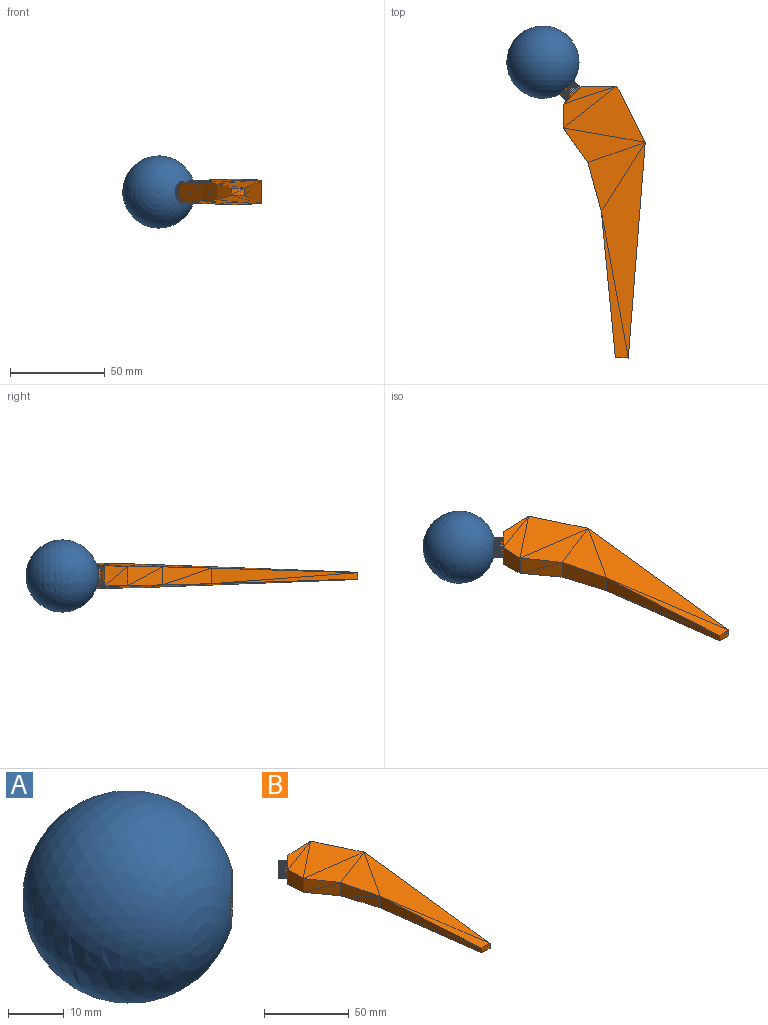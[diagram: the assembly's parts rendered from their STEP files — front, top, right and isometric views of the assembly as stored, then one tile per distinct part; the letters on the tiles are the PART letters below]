
ASSEMBLY  parts=2 mates=1
PART A: 119 faces, bbox 38.1x38.1x38.1 mm
  f0: sphere r=19.05mm, area 4472mm2, adj f2,f3,f4,f5,f6,f7,f8,f9
  f1: plane 10.52x7.44mm, normal (0.71,-0.71,0), area 86.6mm2, adj f2,f3,f4,f5,f6,f7,f8,f9
  f2: plane 0.64x0.63mm, normal (0.69,0.69,0.21), area 0.4mm2, adj f0,f1,f3,f48
  f3: plane 0.58x0.57mm, normal (0.69,0.69,0.21), area 0.1mm2, adj f0,f1,f2,f4
  f4: plane 0.58x0.55mm, normal (0.67,0.67,0.33), area 0mm2, adj f0,f1,f3,f5
  f5: plane 0.75x0.72mm, normal (0.66,0.66,0.35), area 0.5mm2, adj f0,f1,f4,f6
  f6: plane 0.6x0.56mm, normal (0.62,0.62,0.49), area 0mm2, adj f0,f1,f5,f8
  f7: plane 0.84x0.81mm, normal (0.57,0.57,0.6), area 0.5mm2, adj f0,f1,f9,f45
  f8: plane 0.61x0.53mm, normal (0.65,0.68,0.35), area 0mm2, adj f0,f1,f6,f10
  f9: plane 0.62x0.61mm, normal (0.57,0.57,0.6), area 0.1mm2, adj f0,f1,f7,f10
  f10: plane 0.84x0.78mm, normal (0.62,0.62,0.48), area 0.6mm2, adj f0,f1,f8,f9
  f11: plane 0.85x0.82mm, normal (-0.05,-0.05,1), area 0.2mm2, adj f0,f1,f12,f30
  f12: plane 1.07x1.01mm, normal (-0.05,-0.05,1), area 0.5mm2, adj f0,f1,f11,f13
  f13: plane 0.76x0.75mm, normal (-0.09,-0.09,0.99), area 0.1mm2, adj f0,f1,f12,f14
  f14: plane 0.97x0.91mm, normal (-0.15,-0.15,0.98), area 0.3mm2, adj f0,f1,f13,f15
  f15: plane 0.98x0.94mm, normal (-0.15,-0.15,0.98), area 0.4mm2, adj f0,f1,f14,f16
  f16: plane 0.78x0.77mm, normal (-0.21,-0.2,0.96), area 0.1mm2, adj f0,f1,f15,f17
  f17: plane 1.07x1mm, normal (-0.25,-0.25,0.94), area 0.5mm2, adj f0,f1,f16,f18
  f18: plane 0.89x0.87mm, normal (-0.25,-0.25,0.94), area 0.2mm2, adj f0,f1,f17,f19
  f19: plane 0.81x0.77mm, normal (-0.32,-0.32,0.89), area 0.1mm2, adj f0,f1,f18,f20
  f20: plane 1.16x1.07mm, normal (-0.34,-0.34,0.88), area 0.6mm2, adj f0,f1,f19,f22
  f21: plane 1.02x0.99mm, normal (-0.56,-0.57,0.6), area 0.6mm2, adj f0,f1,f23,f101
  f22: plane 0.81x0.8mm, normal (-0.34,-0.34,0.88), area 0.1mm2, adj f0,f1,f20,f24
  f23: plane 0.86x0.84mm, normal (-0.56,-0.57,0.6), area 0.2mm2, adj f0,f1,f21,f25
  f24: plane 0.84x0.76mm, normal (-0.42,-0.42,0.8), area 0.1mm2, adj f0,f1,f22,f26
  f25: plane 0.85x0.8mm, normal (-0.51,-0.51,0.69), area 0.1mm2, adj f0,f1,f23,f27
  f26: plane 1.2x1.11mm, normal (-0.42,-0.42,0.8), area 0.7mm2, adj f0,f1,f24,f28
  f27: plane 1.13x1.07mm, normal (-0.5,-0.5,0.71), area 0.7mm2, adj f0,f1,f25,f28
  f28: plane 0.79x0.78mm, normal (-0.5,-0.5,0.71), area 0mm2, adj f0,f1,f26,f27
  f29: plane 1.14x1.08mm, normal (0.05,0.05,1), area 0.6mm2, adj f0,f1,f30,f31
  f30: plane 0.76x0.71mm, normal (0.03,0.03,1), area 0.1mm2, adj f0,f1,f11,f29
  f31: plane 0.73x0.71mm, normal (0.05,0.05,1), area 0.1mm2, adj f0,f1,f29,f34
  f32: plane 1.17x1.09mm, normal (0.15,0.15,0.98), area 0.6mm2, adj f0,f1,f33,f34
  f33: plane 0.69x0.68mm, normal (0.25,0.25,0.94), area 0.1mm2, adj f0,f1,f32,f35
  f34: plane 0.75x0.68mm, normal (0.15,0.15,0.98), area 0.1mm2, adj f0,f1,f31,f32
  f35: plane 1.1x1.02mm, normal (0.25,0.25,0.94), area 0.6mm2, adj f0,f1,f33,f39
  f36: plane 0.75x0.73mm, normal (0.34,0.34,0.88), area 0.2mm2, adj f0,f1,f37,f39
  f37: plane 0.97x0.9mm, normal (0.34,0.34,0.88), area 0.4mm2, adj f0,f1,f36,f41
  f38: plane 0.8x0.78mm, normal (0.43,0.42,0.8), area 0.3mm2, adj f0,f1,f40,f41
  f39: plane 0.7x0.65mm, normal (0.26,0.27,0.93), area 0.1mm2, adj f0,f1,f35,f36
  f40: plane 0.84x0.8mm, normal (0.43,0.42,0.8), area 0.3mm2, adj f0,f1,f38,f43
  f41: plane 0.66x0.64mm, normal (0.37,0.37,0.85), area 0.1mm2, adj f0,f1,f37,f38
  f42: plane 0.83x0.8mm, normal (0.5,0.5,0.71), area 0.4mm2, adj f0,f1,f43,f44
  f43: plane 0.63x0.63mm, normal (0.46,0.47,0.75), area 0.1mm2, adj f0,f1,f40,f42
  f44: plane 0.72x0.7mm, normal (0.5,0.5,0.71), area 0.2mm2, adj f0,f1,f42,f45
  f45: plane 0.62x0.6mm, normal (0.55,0.55,0.63), area 0.1mm2, adj f0,f1,f7,f44
  f46: plane 0.56x0.56mm, normal (0.71,0.7,0.07), area 0.2mm2, adj f0,f1,f47,f48
  f47: plane 0.57x0.57mm, normal (0.71,0.7,0.07), area 0.3mm2, adj f0,f1,f46,f50
  f48: plane 0.56x0.55mm, normal (0.69,0.7,0.17), area 0mm2, adj f0,f1,f2,f46
  f49: plane 0.57x0.57mm, normal (0.71,0.7,-0.07), area 0.3mm2, adj f0,f1,f50,f51
  f50: plane 0.54x0.54mm, normal (0.7,0.71,0), area 0mm2, adj f0,f1,f47,f49
  f51: plane 0.56x0.56mm, normal (0.71,0.7,-0.07), area 0.2mm2, adj f0,f1,f49,f53
  f52: plane 0.64x0.63mm, normal (0.69,0.69,-0.21), area 0.4mm2, adj f0,f1,f53,f54
  f53: plane 0.55x0.55mm, normal (0.69,0.7,-0.17), area 0mm2, adj f0,f1,f51,f52
  f54: plane 0.57x0.56mm, normal (0.69,0.69,-0.21), area 0.1mm2, adj f0,f1,f52,f56
  f55: plane 0.74x0.71mm, normal (0.66,0.66,-0.35), area 0.5mm2, adj f0,f1,f56,f57
  f56: plane 0.57x0.55mm, normal (0.67,0.67,-0.33), area 0mm2, adj f0,f1,f54,f55
  f57: plane 0.55x0.55mm, normal (0.66,0.66,-0.35), area 0mm2, adj f0,f1,f55,f59
  f58: plane 0.83x0.78mm, normal (0.62,0.62,-0.48), area 0.5mm2, adj f0,f1,f59,f60
  f59: plane 0.59x0.55mm, normal (0.62,0.62,-0.49), area 0mm2, adj f0,f1,f57,f58
  f60: plane 0.61x0.6mm, normal (0.57,0.57,-0.6), area 0.1mm2, adj f0,f1,f58,f61
  f61: plane 0.83x0.8mm, normal (0.57,0.57,-0.6), area 0.5mm2, adj f0,f1,f60,f65
  f62: plane 0.7x0.68mm, normal (0.5,0.5,-0.71), area 0.2mm2, adj f0,f1,f63,f65
  f63: plane 0.82x0.79mm, normal (0.5,0.5,-0.71), area 0.4mm2, adj f0,f1,f62,f67
  f64: plane 0.82x0.78mm, normal (0.43,0.42,-0.8), area 0.3mm2, adj f0,f1,f66,f67
  f65: plane 0.6x0.59mm, normal (0.55,0.55,-0.63), area 0mm2, adj f0,f1,f61,f62
  f66: plane 0.79x0.76mm, normal (0.43,0.42,-0.8), area 0.3mm2, adj f0,f1,f64,f68
  f67: plane 0.61x0.61mm, normal (0.46,0.47,-0.75), area 0.1mm2, adj f0,f1,f63,f64
  f68: plane 0.64x0.62mm, normal (0.37,0.37,-0.85), area 0.1mm2, adj f0,f1,f66,f79
  f69: plane 0.88x0.85mm, normal (-0.25,-0.25,-0.94), area 0.2mm2, adj f0,f1,f70,f109
  f70: plane 1.05x0.98mm, normal (-0.25,-0.25,-0.94), area 0.5mm2, adj f0,f1,f69,f71
  f71: plane 0.76x0.74mm, normal (-0.21,-0.2,-0.96), area 0.1mm2, adj f0,f1,f70,f72
  f72: plane 0.96x0.92mm, normal (-0.15,-0.15,-0.98), area 0.3mm2, adj f0,f1,f71,f73
  f73: plane 0.95x0.89mm, normal (-0.15,-0.15,-0.98), area 0.3mm2, adj f0,f1,f72,f74
  f74: plane 0.74x0.73mm, normal (-0.09,-0.09,-0.99), area 0.1mm2, adj f0,f1,f73,f75
  f75: plane 1.04x0.99mm, normal (-0.05,-0.05,-1), area 0.5mm2, adj f0,f1,f74,f76
  f76: plane 0.83x0.8mm, normal (-0.05,-0.05,-1), area 0.2mm2, adj f0,f1,f75,f77
  f77: plane 0.74x0.69mm, normal (0.03,0.03,-1), area 0.1mm2, adj f0,f1,f76,f78
  f78: plane 1.12x1.06mm, normal (0.05,0.05,-1), area 0.6mm2, adj f0,f1,f77,f80
  f79: plane 0.95x0.89mm, normal (0.34,0.34,-0.88), area 0.4mm2, adj f0,f1,f68,f81
  f80: plane 0.7x0.69mm, normal (0.05,0.05,-1), area 0.1mm2, adj f0,f1,f78,f82
  f81: plane 0.73x0.72mm, normal (0.34,0.34,-0.88), area 0.2mm2, adj f0,f1,f79,f83
  f82: plane 0.73x0.65mm, normal (0.15,0.15,-0.98), area 0.1mm2, adj f0,f1,f80,f84
  f83: plane 0.68x0.63mm, normal (0.26,0.27,-0.93), area 0.1mm2, adj f0,f1,f81,f85
  f84: plane 1.15x1.08mm, normal (0.15,0.15,-0.98), area 0.6mm2, adj f0,f1,f82,f86
  f85: plane 1.08x1mm, normal (0.25,0.25,-0.94), area 0.6mm2, adj f0,f1,f83,f86
  f86: plane 0.67x0.66mm, normal (0.25,0.25,-0.94), area 0mm2, adj f0,f1,f84,f85
  f87: plane 0.9x0.87mm, normal (-0.69,-0.69,-0.21), area 0.6mm2, adj f0,f1,f88,f118
  f88: plane 0.82x0.82mm, normal (-0.69,-0.69,-0.21), area 0.1mm2, adj f0,f1,f87,f89
  f89: plane 0.81x0.8mm, normal (-0.71,-0.7,-0.08), area 0.1mm2, adj f0,f1,f88,f90
  f90: plane 0.85x0.84mm, normal (-0.71,-0.71,-0.07), area 0.8mm2, adj f0,f1,f89,f92
  f91: plane 0.82x0.82mm, normal (-0.69,-0.69,0.21), area 0.1mm2, adj f0,f1,f93,f94
  f92: plane 0.84x0.84mm, normal (-0.71,-0.71,0.07), area 0.8mm2, adj f0,f1,f90,f94
  f93: plane 0.9x0.88mm, normal (-0.69,-0.69,0.21), area 0.6mm2, adj f0,f1,f91,f96
  f94: plane 0.81x0.81mm, normal (-0.71,-0.7,0.08), area 0.1mm2, adj f0,f1,f91,f92
  f95: plane 0.87x0.86mm, normal (-0.66,-0.66,0.35), area 0.3mm2, adj f0,f1,f96,f97
  f96: plane 0.82x0.81mm, normal (-0.69,-0.68,0.25), area 0.1mm2, adj f0,f1,f93,f95
  f97: plane 0.92x0.89mm, normal (-0.66,-0.66,0.35), area 0.5mm2, adj f0,f1,f95,f100
  f98: plane 0.94x0.92mm, normal (-0.62,-0.62,0.48), area 0.4mm2, adj f0,f1,f99,f100
  f99: plane 0.91x0.88mm, normal (-0.62,-0.62,0.48), area 0.3mm2, adj f0,f1,f98,f101
  f100: plane 0.82x0.82mm, normal (-0.65,-0.64,0.41), area 0.1mm2, adj f0,f1,f97,f98
  f101: plane 0.83x0.81mm, normal (-0.59,-0.58,0.56), area 0.1mm2, adj f0,f1,f21,f99
  f102: plane 0.8x0.79mm, normal (-0.34,-0.34,-0.88), area 0.1mm2, adj f0,f1,f103,f105
  f103: plane 1.17x1.09mm, normal (-0.42,-0.42,-0.8), area 0.7mm2, adj f0,f1,f102,f108
  f104: plane 0.77x0.77mm, normal (-0.5,-0.5,-0.71), area 0mm2, adj f0,f1,f106,f108
  f105: plane 1.14x1.06mm, normal (-0.34,-0.34,-0.88), area 0.6mm2, adj f0,f1,f102,f109
  f106: plane 1.11x1.06mm, normal (-0.5,-0.5,-0.71), area 0.7mm2, adj f0,f1,f104,f111
  f107: plane 0.85x0.83mm, normal (-0.56,-0.57,-0.6), area 0.2mm2, adj f0,f1,f110,f111
  f108: plane 0.84x0.76mm, normal (-0.42,-0.42,-0.8), area 0.1mm2, adj f0,f1,f103,f104
  f109: plane 0.79x0.75mm, normal (-0.32,-0.32,-0.89), area 0.1mm2, adj f0,f1,f69,f105
  f110: plane 1.01x0.98mm, normal (-0.56,-0.57,-0.6), area 0.6mm2, adj f0,f1,f107,f113
  f111: plane 0.83x0.78mm, normal (-0.51,-0.51,-0.69), area 0.1mm2, adj f0,f1,f106,f107
  f112: plane 0.9x0.87mm, normal (-0.62,-0.62,-0.48), area 0.3mm2, adj f0,f1,f113,f114
  f113: plane 0.82x0.8mm, normal (-0.59,-0.58,-0.56), area 0.1mm2, adj f0,f1,f110,f112
  f114: plane 0.93x0.91mm, normal (-0.62,-0.62,-0.48), area 0.4mm2, adj f0,f1,f112,f117
  f115: plane 0.91x0.88mm, normal (-0.66,-0.66,-0.35), area 0.5mm2, adj f0,f1,f116,f117
  f116: plane 0.86x0.85mm, normal (-0.66,-0.66,-0.35), area 0.3mm2, adj f0,f1,f115,f118
  f117: plane 0.81x0.81mm, normal (-0.65,-0.64,-0.41), area 0.1mm2, adj f0,f1,f114,f115
  f118: plane 0.82x0.81mm, normal (-0.69,-0.68,-0.25), area 0.1mm2, adj f0,f1,f87,f116
PART B: 189 faces, bbox 45.8x146.9x13.4 mm
  f0: plane 10.52x7.44mm, normal (-0.71,0.71,0), area 86.6mm2, adj f1,f2,f3,f4,f5,f6,f7,f8
  f1: plane 4.22x4.14mm, normal (-0.69,-0.69,-0.21), area 1.7mm2, adj f0,f2,f47
  f2: plane 4.17x4.13mm, normal (-0.69,-0.69,-0.21), area 0.5mm2, adj f0,f1,f3
  f3: plane 4.32x4.17mm, normal (-0.67,-0.67,-0.33), area 2.6mm2, adj f0,f2,f4,f137
  f4: plane 4.32x4.14mm, normal (-0.66,-0.66,-0.35), area 2.1mm2, adj f0,f3,f5
  f5: plane 4.44x4.14mm, normal (-0.62,-0.62,-0.49), area 2.6mm2, adj f0,f4,f7,f136
  f6: plane 4.41x4.13mm, normal (-0.57,-0.57,-0.6), area 1.8mm2, adj f0,f8,f44
  f7: plane 4.44x3.84mm, normal (-0.65,-0.68,-0.35), area 0.1mm2, adj f0,f5,f9
  f8: plane 4.18x4.14mm, normal (-0.57,-0.57,-0.6), area 0.4mm2, adj f0,f6,f9
  f9: plane 4.44x4.09mm, normal (-0.62,-0.62,-0.48), area 2.2mm2, adj f0,f7,f8
  f10: plane 4.29x4.14mm, normal (0.05,0.05,-1), area 0.7mm2, adj f0,f11,f29
  f11: plane 4.51x4.14mm, normal (0.05,0.05,-1), area 1.5mm2, adj f0,f10,f12
  f12: plane 4.51x4.39mm, normal (0.09,0.09,-0.99), area 2.6mm2, adj f0,f11,f13,f163
  f13: plane 4.39x4.13mm, normal (0.15,0.15,-0.98), area 1.1mm2, adj f0,f12,f14
  f14: plane 4.4x4.14mm, normal (0.15,0.15,-0.98), area 1.1mm2, adj f0,f13,f15
  f15: plane 4.48x4.4mm, normal (0.21,0.2,-0.96), area 2.6mm2, adj f0,f14,f16,f165
  f16: plane 4.48x4.13mm, normal (0.25,0.25,-0.94), area 1.5mm2, adj f0,f15,f17
  f17: plane 4.29x4.14mm, normal (0.25,0.25,-0.94), area 0.7mm2, adj f0,f16,f18
  f18: plane 4.54x4.3mm, normal (0.32,0.32,-0.89), area 2.6mm2, adj f0,f17,f19,f164
  f19: plane 4.54x4.13mm, normal (0.34,0.34,-0.88), area 1.9mm2, adj f0,f18,f21
  f20: plane 4.37x4.14mm, normal (0.56,0.57,-0.6), area 1.7mm2, adj f0,f22,f100
  f21: plane 4.2x4.14mm, normal (0.34,0.34,-0.88), area 0.3mm2, adj f0,f19,f23
  f22: plane 4.22x4.13mm, normal (0.56,0.57,-0.6), area 0.5mm2, adj f0,f20,f24
  f23: plane 4.58x4.2mm, normal (0.42,0.42,-0.8), area 2.6mm2, adj f0,f21,f25,f162
  f24: plane 4.49x4.22mm, normal (0.51,0.51,-0.69), area 2.6mm2, adj f0,f22,f26,f161
  f25: plane 4.58x4.12mm, normal (0.42,0.42,-0.8), area 2.2mm2, adj f0,f23,f27
  f26: plane 4.49x4.14mm, normal (0.5,0.5,-0.71), area 2.1mm2, adj f0,f24,f27
  f27: plane 4.16x4.14mm, normal (0.5,0.5,-0.71), area 0.1mm2, adj f0,f25,f26
  f28: plane 4.61x4.14mm, normal (-0.05,-0.05,-1), area 2mm2, adj f0,f29,f30
  f29: plane 4.61x4.29mm, normal (-0.03,-0.03,-1), area 2.6mm2, adj f0,f10,f28,f129
  f30: plane 4.19x4.14mm, normal (-0.05,-0.05,-1), area 0.2mm2, adj f0,f28,f33
  f31: plane 4.7x4.1mm, normal (-0.15,-0.15,-0.98), area 2.2mm2, adj f0,f32,f33
  f32: plane 4.18x4.14mm, normal (-0.25,-0.25,-0.94), area 0.2mm2, adj f0,f31,f34
  f33: plane 4.7x4.19mm, normal (-0.15,-0.15,-0.98), area 2.6mm2, adj f0,f30,f31,f131
  f34: plane 4.59x4.14mm, normal (-0.25,-0.25,-0.94), area 2mm2, adj f0,f32,f38
  f35: plane 4.27x4.13mm, normal (-0.34,-0.34,-0.88), area 0.6mm2, adj f0,f36,f38
  f36: plane 4.47x4.14mm, normal (-0.34,-0.34,-0.88), area 1.6mm2, adj f0,f35,f40
  f37: plane 4.34x4.13mm, normal (-0.43,-0.42,-0.8), area 1mm2, adj f0,f39,f40
  f38: plane 4.59x4.27mm, normal (-0.26,-0.27,-0.93), area 2.6mm2, adj f0,f34,f35,f132
  f39: plane 4.36x4.14mm, normal (-0.43,-0.42,-0.8), area 1.2mm2, adj f0,f37,f42
  f40: plane 4.47x4.34mm, normal (-0.37,-0.37,-0.85), area 2.6mm2, adj f0,f36,f37,f133
  f41: plane 4.39x4.13mm, normal (-0.5,-0.5,-0.71), area 1.4mm2, adj f0,f42,f43
  f42: plane 4.39x4.36mm, normal (-0.46,-0.47,-0.75), area 2.6mm2, adj f0,f39,f41,f134
  f43: plane 4.26x4.14mm, normal (-0.5,-0.5,-0.71), area 0.8mm2, adj f0,f41,f44
  f44: plane 4.41x4.26mm, normal (-0.55,-0.55,-0.63), area 2.6mm2, adj f0,f6,f43,f135
  f45: plane 4.16x4.13mm, normal (-0.71,-0.7,-0.07), area 0.9mm2, adj f0,f46,f47
  f46: plane 4.15x4.15mm, normal (-0.71,-0.7,-0.07), area 1.3mm2, adj f0,f45,f49
  f47: plane 4.22x4.16mm, normal (-0.69,-0.7,-0.17), area 2.6mm2, adj f0,f1,f45,f138
  f48: plane 4.15x4.15mm, normal (-0.71,-0.7,0.07), area 1.3mm2, adj f0,f49,f50
  f49: plane 4.15x4.12mm, normal (-0.7,-0.71,0), area 2.6mm2, adj f0,f46,f48,f139
  f50: plane 4.16x4.13mm, normal (-0.71,-0.7,0.07), area 0.9mm2, adj f0,f48,f52
  f51: plane 4.22x4.14mm, normal (-0.69,-0.69,0.21), area 1.7mm2, adj f0,f52,f53
  f52: plane 4.22x4.16mm, normal (-0.69,-0.7,0.17), area 2.6mm2, adj f0,f50,f51,f141
  f53: plane 4.17x4.13mm, normal (-0.69,-0.69,0.21), area 0.5mm2, adj f0,f51,f55
  f54: plane 4.32x4.14mm, normal (-0.66,-0.66,0.35), area 2.1mm2, adj f0,f55,f56
  f55: plane 4.32x4.17mm, normal (-0.67,-0.67,0.33), area 2.6mm2, adj f0,f53,f54,f142
  f56: plane 4.14x4.14mm, normal (-0.66,-0.66,0.35), area 0.1mm2, adj f0,f54,f58
  f57: plane 4.44x4.09mm, normal (-0.62,-0.62,0.48), area 2.2mm2, adj f0,f58,f59
  f58: plane 4.44x4.14mm, normal (-0.62,-0.62,0.49), area 2.6mm2, adj f0,f56,f57,f143
  f59: plane 4.18x4.14mm, normal (-0.57,-0.57,0.6), area 0.4mm2, adj f0,f57,f60
  f60: plane 4.41x4.13mm, normal (-0.57,-0.57,0.6), area 1.8mm2, adj f0,f59,f64
  f61: plane 4.26x4.14mm, normal (-0.5,-0.5,0.71), area 0.8mm2, adj f0,f62,f64
  f62: plane 4.39x4.13mm, normal (-0.5,-0.5,0.71), area 1.4mm2, adj f0,f61,f66
  f63: plane 4.36x4.14mm, normal (-0.43,-0.42,0.8), area 1.2mm2, adj f0,f65,f66
  f64: plane 4.41x4.26mm, normal (-0.55,-0.55,0.63), area 2.6mm2, adj f0,f60,f61,f144
  f65: plane 4.34x4.13mm, normal (-0.43,-0.42,0.8), area 1mm2, adj f0,f63,f67
  f66: plane 4.39x4.36mm, normal (-0.46,-0.47,0.75), area 2.6mm2, adj f0,f62,f63,f146
  f67: plane 4.47x4.34mm, normal (-0.37,-0.37,0.85), area 2.6mm2, adj f0,f65,f78,f147
  f68: plane 4.29x4.14mm, normal (0.25,0.25,0.94), area 0.7mm2, adj f0,f69,f108
  f69: plane 4.48x4.13mm, normal (0.25,0.25,0.94), area 1.5mm2, adj f0,f68,f70
  f70: plane 4.48x4.4mm, normal (0.21,0.2,0.96), area 2.6mm2, adj f0,f69,f71,f175
  f71: plane 4.4x4.14mm, normal (0.15,0.15,0.98), area 1.1mm2, adj f0,f70,f72
  f72: plane 4.39x4.13mm, normal (0.15,0.15,0.98), area 1.1mm2, adj f0,f71,f73
  f73: plane 4.51x4.39mm, normal (0.09,0.09,0.99), area 2.6mm2, adj f0,f72,f74,f177
  f74: plane 4.51x4.14mm, normal (0.05,0.05,1), area 1.5mm2, adj f0,f73,f75
  f75: plane 4.29x4.14mm, normal (0.05,0.05,1), area 0.7mm2, adj f0,f74,f76
  f76: plane 4.61x4.29mm, normal (-0.03,-0.03,1), area 2.6mm2, adj f0,f75,f77,f180
  f77: plane 4.61x4.14mm, normal (-0.05,-0.05,1), area 2mm2, adj f0,f76,f79
  f78: plane 4.47x4.14mm, normal (-0.34,-0.34,0.88), area 1.6mm2, adj f0,f67,f80
  f79: plane 4.19x4.14mm, normal (-0.05,-0.05,1), area 0.2mm2, adj f0,f77,f81
  f80: plane 4.27x4.13mm, normal (-0.34,-0.34,0.88), area 0.6mm2, adj f0,f78,f82
  f81: plane 4.7x4.19mm, normal (-0.15,-0.15,0.98), area 2.6mm2, adj f0,f79,f83,f179
  f82: plane 4.59x4.27mm, normal (-0.26,-0.27,0.93), area 2.6mm2, adj f0,f80,f84,f145
  f83: plane 4.7x4.1mm, normal (-0.15,-0.15,0.98), area 2.2mm2, adj f0,f81,f85
  f84: plane 4.59x4.14mm, normal (-0.25,-0.25,0.94), area 2mm2, adj f0,f82,f85
  f85: plane 4.18x4.14mm, normal (-0.25,-0.25,0.94), area 0.2mm2, adj f0,f83,f84
  f86: plane 4.23x4.13mm, normal (0.69,0.69,0.21), area 1.8mm2, adj f0,f87,f117
  f87: plane 4.15x4.14mm, normal (0.69,0.69,0.21), area 0.4mm2, adj f0,f86,f88
  f88: plane 4.17x4.15mm, normal (0.71,0.7,0.08), area 2.6mm2, adj f0,f87,f89,f183
  f89: plane 4.17x4.14mm, normal (0.71,0.71,0.07), area 2.2mm2, adj f0,f88,f91
  f90: plane 4.15x4.14mm, normal (0.69,0.69,-0.21), area 0.4mm2, adj f0,f92,f93
  f91: plane 4.17x4.14mm, normal (0.71,0.71,-0.07), area 2.2mm2, adj f0,f89,f93
  f92: plane 4.23x4.13mm, normal (0.69,0.69,-0.21), area 1.8mm2, adj f0,f90,f95
  f93: plane 4.17x4.15mm, normal (0.71,0.7,-0.08), area 2.6mm2, adj f0,f90,f91,f157
  f94: plane 4.2x4.15mm, normal (0.66,0.66,-0.35), area 0.8mm2, adj f0,f95,f96
  f95: plane 4.23x4.2mm, normal (0.69,0.68,-0.25), area 2.6mm2, adj f0,f92,f94,f158
  f96: plane 4.26x4.13mm, normal (0.66,0.66,-0.35), area 1.4mm2, adj f0,f94,f99
  f97: plane 4.27x4.14mm, normal (0.62,0.62,-0.48), area 1.2mm2, adj f0,f98,f99
  f98: plane 4.25x4.13mm, normal (0.62,0.62,-0.48), area 0.9mm2, adj f0,f97,f100
  f99: plane 4.27x4.26mm, normal (0.65,0.64,-0.41), area 2.6mm2, adj f0,f96,f97,f159
  f100: plane 4.37x4.26mm, normal (0.59,0.58,-0.56), area 2.6mm2, adj f0,f20,f98,f160
  f101: plane 4.2x4.14mm, normal (0.34,0.34,0.88), area 0.3mm2, adj f0,f102,f104
  f102: plane 4.62x4.08mm, normal (0.42,0.42,0.8), area 2.2mm2, adj f0,f101,f107
  f103: plane 4.16x4.14mm, normal (0.5,0.5,0.71), area 0.1mm2, adj f0,f105,f107
  f104: plane 4.54x4.13mm, normal (0.34,0.34,0.88), area 1.9mm2, adj f0,f101,f108
  f105: plane 4.49x4.14mm, normal (0.5,0.5,0.71), area 2.1mm2, adj f0,f103,f110
  f106: plane 4.22x4.13mm, normal (0.56,0.57,0.6), area 0.5mm2, adj f0,f109,f110
  f107: plane 4.62x4.16mm, normal (0.42,0.42,0.8), area 2.6mm2, adj f0,f102,f103,f172
  f108: plane 4.54x4.3mm, normal (0.32,0.32,0.89), area 2.6mm2, adj f0,f68,f104,f173
  f109: plane 4.37x4.14mm, normal (0.56,0.57,0.6), area 1.7mm2, adj f0,f106,f112
  f110: plane 4.49x4.22mm, normal (0.51,0.51,0.69), area 2.6mm2, adj f0,f105,f106,f174
  f111: plane 4.25x4.13mm, normal (0.62,0.62,0.48), area 0.9mm2, adj f0,f112,f113
  f112: plane 4.37x4.26mm, normal (0.59,0.58,0.56), area 2.6mm2, adj f0,f109,f111,f176
  f113: plane 4.27x4.14mm, normal (0.62,0.62,0.48), area 1.2mm2, adj f0,f111,f116
  f114: plane 4.26x4.13mm, normal (0.66,0.66,0.35), area 1.4mm2, adj f0,f115,f116
  f115: plane 4.2x4.15mm, normal (0.66,0.66,0.35), area 0.8mm2, adj f0,f114,f117
  f116: plane 4.27x4.26mm, normal (0.65,0.64,0.41), area 2.6mm2, adj f0,f113,f114,f178
  f117: plane 4.23x4.2mm, normal (0.69,0.68,0.25), area 2.6mm2, adj f0,f86,f115,f181
  f118: plane 113.68x23.12mm, normal (-0.03,-0.03,-1), area 1027.1mm2, adj f120,f122,f126
  f119: plane 77.03x8.22mm, normal (-1,-0.1,0), area 318mm2, adj f120,f121,f128
  f120: plane 77.03x7.39mm, normal (-1,-0.1,0), area 129.7mm2, adj f118,f119,f123
  f121: plane 77.03x14.22mm, normal (-0.03,-0.03,1), area 263.3mm2, adj f119,f123,f148
  f122: plane 113.68x15.72mm, normal (-0.03,-0.03,-1), area 388.5mm2, adj f118,f124,f151
  f123: plane 6.83x3.59mm, normal (0,-1,0), area 11.4mm2, adj f120,f121,f124
  f124: plane 6.83x3.83mm, normal (0,-1,0), area 13.1mm2, adj f122,f123,f150
  f125: plane 36.65x30.23mm, normal (-0.03,-0.03,1), area 430.7mm2, adj f127,f148,f153
  f126: plane 36.65x30.23mm, normal (-0.03,-0.03,-1), area 430.7mm2, adj f118,f128,f152
  f127: plane 25.94x9.54mm, normal (-0.96,-0.26,0), area 128.2mm2, adj f125,f128,f156
  f128: plane 25.94x8.88mm, normal (-0.96,-0.26,0), area 110.5mm2, adj f119,f126,f127
  f129: plane 4.75x4.75mm, normal (-0.71,0.71,0), area 0.2mm2, adj f29,f130,f163
  f130: plane 9.51x9.51mm, normal (-0.71,0.71,0), area 3.4mm2, adj f129,f131,f169
  f131: plane 4.76x4.76mm, normal (-0.71,0.71,0), area 0.7mm2, adj f33,f130,f132
  f132: plane 4.15x4.15mm, normal (-0.71,0.71,0), area 1.1mm2, adj f38,f131,f133
  f133: plane 3.56x3.56mm, normal (-0.71,0.71,0), area 1.4mm2, adj f40,f132,f134
  f134: plane 3.03x3.03mm, normal (-0.71,0.71,0), area 1.7mm2, adj f42,f133,f135
  f135: plane 2.55x2.55mm, normal (-0.71,0.71,0), area 1.7mm2, adj f44,f134,f136
  f136: plane 3.23x2.16mm, normal (-0.71,0.71,0), area 1.7mm2, adj f5,f135,f137
  f137: plane 4.07x1.85mm, normal (-0.71,0.71,0), area 1.6mm2, adj f3,f136,f138
  f138: plane 4.95x1.64mm, normal (-0.71,0.71,0), area 1.3mm2, adj f47,f137,f139
  f139: plane 5.84x1.53mm, normal (-0.71,0.71,0), area 1mm2, adj f49,f138,f140
  f140: plane 10.78x1.53mm, normal (-0.71,0.71,0), area 11.7mm2, adj f139,f141,f170
  f141: plane 4.95x1.64mm, normal (-0.71,0.71,0), area 1.3mm2, adj f52,f140,f142
  f142: plane 4.07x1.85mm, normal (-0.71,0.71,0), area 1.6mm2, adj f55,f141,f143
  f143: plane 3.23x2.16mm, normal (-0.71,0.71,0), area 1.7mm2, adj f58,f142,f144
  f144: plane 2.55x2.55mm, normal (-0.71,0.71,0), area 1.7mm2, adj f64,f143,f146
  f145: plane 4.15x4.15mm, normal (-0.71,0.71,0), area 1.1mm2, adj f82,f147,f179
  f146: plane 3.03x3.03mm, normal (-0.71,0.71,0), area 1.7mm2, adj f66,f144,f147
  f147: plane 3.56x3.56mm, normal (-0.71,0.71,0), area 1.4mm2, adj f67,f145,f146
  f148: plane 113.68x23.12mm, normal (-0.03,-0.03,1), area 1152.4mm2, adj f121,f125,f150
  f149: plane 29.65x14.87mm, normal (0.89,0.45,0), area 205.5mm2, adj f151,f166,f185
  f150: plane 113.68x8.9mm, normal (1,-0.08,0), area 218.3mm2, adj f124,f148,f151
  f151: plane 113.68x12.39mm, normal (1,-0.08,0), area 706.6mm2, adj f122,f149,f150
  f152: plane 40.36x30.23mm, normal (-0.03,-0.03,-1), area 528.4mm2, adj f126,f154,f185
  f153: plane 43.2x18.26mm, normal (-0.03,-0.03,1), area 345.8mm2, adj f125,f155,f166
  f154: plane 40.36x28.33mm, normal (-0.03,-0.03,-1), area 402.4mm2, adj f152,f156,f167
  f155: plane 18.26x12.97mm, normal (-0.82,-0.58,0), area 110.9mm2, adj f153,f156,f171
  f156: plane 18.26x12.97mm, normal (-0.82,-0.58,0), area 106.8mm2, adj f127,f154,f155
  f157: plane 6.06x0.61mm, normal (-0.71,0.71,0), area 0.6mm2, adj f93,f158,f186
  f158: plane 5.17x0.77mm, normal (-0.71,0.71,0), area 1mm2, adj f95,f157,f159
  f159: plane 4.31x1.03mm, normal (-0.71,0.71,0), area 1.2mm2, adj f99,f158,f160
  f160: plane 3.49x1.38mm, normal (-0.71,0.71,0), area 1.4mm2, adj f100,f159,f161
  f161: plane 2.75x1.82mm, normal (-0.71,0.71,0), area 1.5mm2, adj f24,f160,f162
  f162: plane 2.33x2.33mm, normal (-0.71,0.71,0), area 1.4mm2, adj f23,f161,f164
  f163: plane 4.12x4.12mm, normal (-0.71,0.71,0), area 0.7mm2, adj f12,f129,f165
  f164: plane 2.89x2.89mm, normal (-0.71,0.71,0), area 1.3mm2, adj f18,f162,f165
  f165: plane 3.49x3.49mm, normal (-0.71,0.71,0), area 1mm2, adj f15,f163,f164
  f166: plane 43.2x29.65mm, normal (-0.03,-0.03,1), area 585mm2, adj f149,f153,f168
  f167: plane 28.33x22.1mm, normal (-0.03,-0.03,-1), area 208.2mm2, adj f154,f169,f188
  f168: plane 28.33x22.1mm, normal (-0.03,-0.03,1), area 178.5mm2, adj f166,f170,f184
  f169: plane 22.1x9.51mm, normal (-0.03,-0.03,-1), area 59.9mm2, adj f130,f167,f171
  f170: plane 12.59x10.78mm, normal (-1,0,0), area 67.9mm2, adj f140,f168,f171
  f171: plane 12.59x10.34mm, normal (-1,0,0), area 62.3mm2, adj f155,f169,f170
  f172: plane 2.33x2.33mm, normal (-0.71,0.71,0), area 1.4mm2, adj f107,f173,f174
  f173: plane 2.89x2.89mm, normal (-0.71,0.71,0), area 1.3mm2, adj f108,f172,f175
  f174: plane 2.75x1.82mm, normal (-0.71,0.71,0), area 1.5mm2, adj f110,f172,f176
  f175: plane 3.49x3.49mm, normal (-0.71,0.71,0), area 1mm2, adj f70,f173,f177
  f176: plane 3.49x1.38mm, normal (-0.71,0.71,0), area 1.4mm2, adj f112,f174,f178
  f177: plane 4.12x4.12mm, normal (-0.71,0.71,0), area 0.7mm2, adj f73,f175,f180
  f178: plane 4.31x1.03mm, normal (-0.71,0.71,0), area 1.2mm2, adj f116,f176,f181
  f179: plane 4.76x4.76mm, normal (-0.71,0.71,0), area 0.7mm2, adj f81,f145,f182
  f180: plane 4.75x4.75mm, normal (-0.71,0.71,0), area 0.2mm2, adj f76,f177,f182
  f181: plane 5.17x0.77mm, normal (-0.71,0.71,0), area 1mm2, adj f117,f178,f183
  f182: plane 9.51x9.51mm, normal (-0.71,0.71,0), area 3.4mm2, adj f179,f180,f184
  f183: plane 6.06x0.61mm, normal (-0.71,0.71,0), area 0.6mm2, adj f88,f181,f186
  f184: plane 28.33x9.51mm, normal (-0.03,-0.03,1), area 89.6mm2, adj f168,f182,f187
  f185: plane 29.65x14.87mm, normal (0.89,0.45,0), area 222.7mm2, adj f149,f152,f187
  f186: plane 12.11x0.56mm, normal (-0.71,0.71,0), area 4.8mm2, adj f157,f183,f188
  f187: plane 18.82x13.43mm, normal (0,1,0), area 126.4mm2, adj f184,f185,f188
  f188: plane 18.82x12.77mm, normal (0,1,0), area 114mm2, adj f167,f186,f187
PLACE A t=(-7.32,83.99,-16.59)mm
PLACE B rot(axis=(0.71,-0.71,0),0deg) t=(-52800.73,-109732.3,-19066.54)mm
MATE parallel A.f1 <-> B.f0  axis (0.71,-0.71,0) through (4.5,71.27,-16.54)mm
